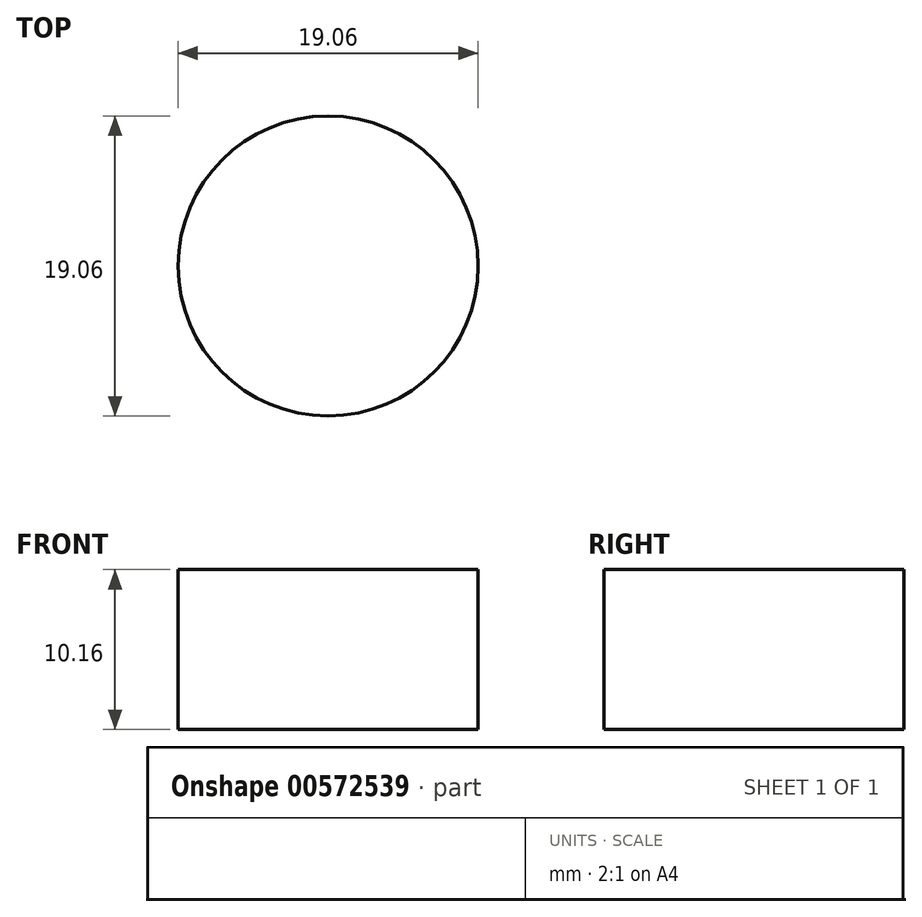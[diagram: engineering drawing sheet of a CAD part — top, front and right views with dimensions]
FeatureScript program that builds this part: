
annotation { "Feature Type Name" : "Feature", "Feature Type Description" : "" }
export const myFeature = defineFeature(function(context is Context, id is Id, definition is map)
    precondition{}
    {
        {
            var Q0;
            Q0=qCreatedBy(makeId("Top.planeOp"),FACE);
            var sketch = newSketch(context, id + "F0", { "sketchPlane" : qUnion([Q0])});
            skCircle(sketch, "E0", {"center": v(0, 0) * mm, "radius": 9.53 * mm});
            skSolve(sketch);
        }
        {
            var Q0;
            Q0=makeQuery(id+"F0.imprint","IMPRINT",FACE,{"disambiguationData":[TD([[makeQuery(id+"F0.imprint","IMPRINT",EDGE,{"derivedFrom":sQuery(id+"F0.wireOp",EDGE,"E0")}),1.0]])]});
            var Q1;
            Q1=sQuery(id+"F0.wireOp",EDGE,"E0");
            extrude(context, id + "F1", {"entities" : qUnion([Q0]), "surfaceEntities" : qUnion([Q1]), "depth" : 10.16 * mm, "offsetDistance" : 25.4 * mm});
        }
    });
